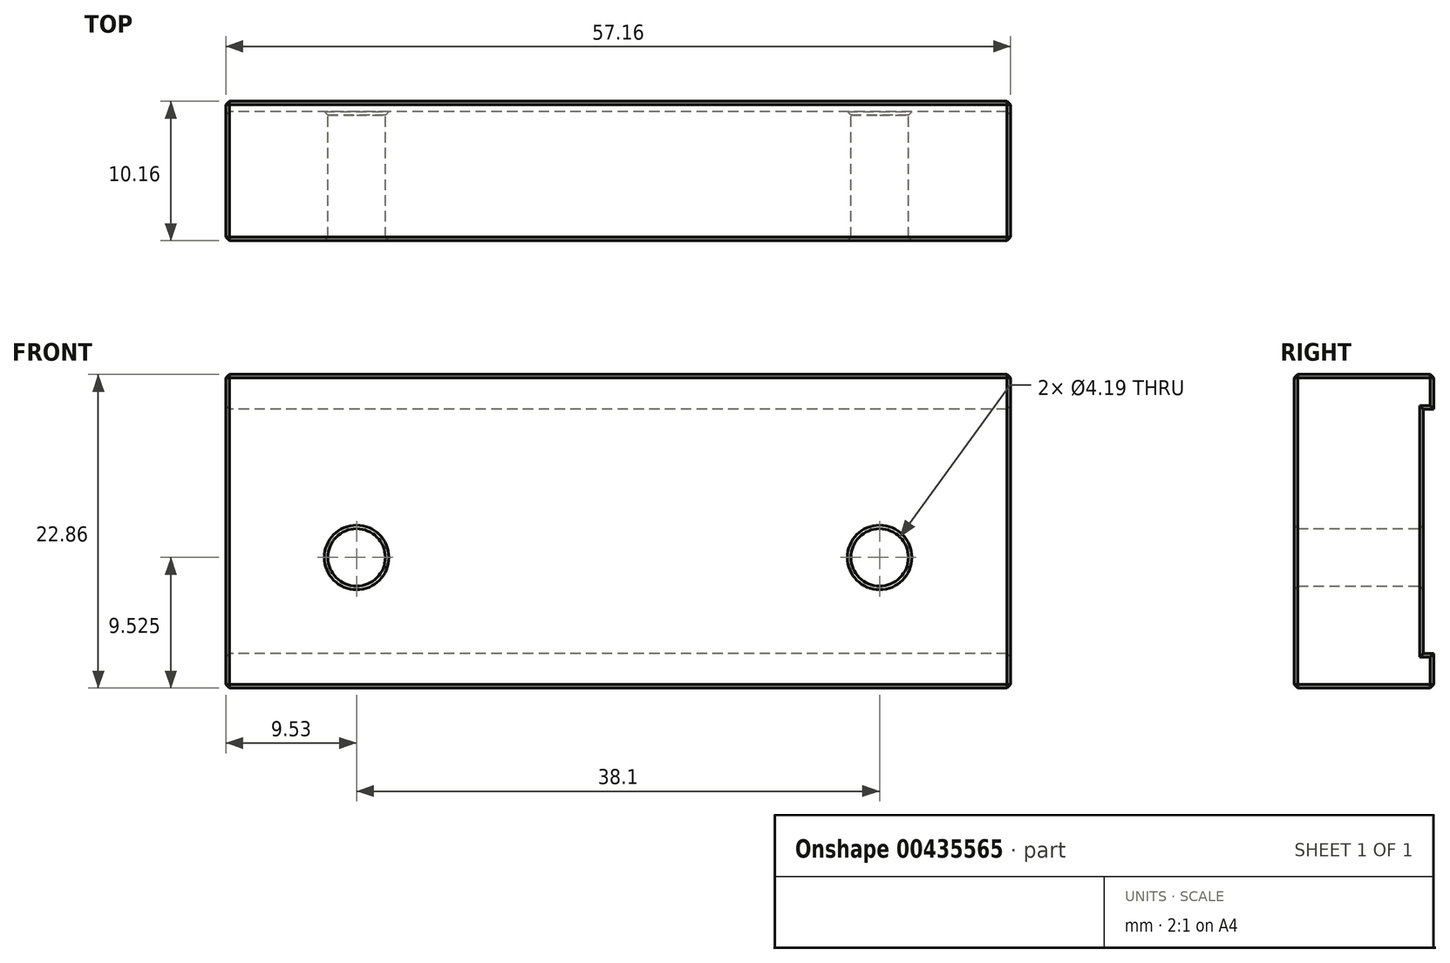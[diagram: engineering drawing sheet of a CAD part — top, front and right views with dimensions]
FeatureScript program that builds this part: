
annotation { "Feature Type Name" : "Feature", "Feature Type Description" : "" }
export const myFeature = defineFeature(function(context is Context, id is Id, definition is map)
    precondition{}
    {
        {
            var Q0;
            Q0=qCreatedBy(makeId("Front.planeOp"),FACE);
            var sketch = newSketch(context, id + "F0", { "sketchPlane" : qUnion([Q0])});
            skLineSegment(sketch, "E0.bottom", {"start": v(28.58, -11.43) * mm, "end": v(-28.58, -11.43) * mm});
            skLineSegment(sketch, "E0.top", {"start": v(28.58, 11.43) * mm, "end": v(-28.58, 11.43) * mm});
            skLineSegment(sketch, "E0.left", {"start": v(28.58, -11.43) * mm, "end": v(28.58, 11.43) * mm});
            skLineSegment(sketch, "E0.right", {"start": v(-28.58, -11.43) * mm, "end": v(-28.58, 11.43) * mm});
            skPoint(sketch, "E0.middle", {"position": v(0, 0) * mm});
            skCircle(sketch, "E1", {"center": v(-19.05, -1.9) * mm, "radius": 2.1 * mm});
            skCircle(sketch, "E2.MirrorC", {"center": v(19.05, -1.9) * mm, "radius": 2.1 * mm});
            skSolve(sketch);
        }
        {
            var Q0;
            Q0=makeQuery(id+"F0.imprint","IMPRINT",FACE,{"disambiguationData":[TD([[makeQuery(id+"F0.imprint","IMPRINT",EDGE,{"derivedFrom":sQuery(id+"F0.wireOp",EDGE,"E0.bottom")}),-1.0]])]});
            extrude(context, id + "F1", {"entities" : qUnion([Q0]), "depth" : 9.4 * mm});
        }
        {
            var Q0;
            Q0=makeQuery(id+"F1.opExtrude","CAP_FACE",FACE,{"disambiguationData":[OSD([sQuery(id+"F0.wireOp",EDGE,"E0.bottom"),sQuery(id+"F0.wireOp",EDGE,"E0.top"),sQuery(id+"F0.wireOp",EDGE,"E0.left"),sQuery(id+"F0.wireOp",EDGE,"E0.right"),sQuery(id+"F0.wireOp",EDGE,"E1"),sQuery(id+"F0.wireOp",EDGE,"E2.MirrorC")])],"isStart":true});
            var sketch = newSketch(context, id + "F2", { "sketchPlane" : qUnion([Q0])});
            skLineSegment(sketch, "E3.bottom", {"start": v(-28.58, -11.43) * mm, "end": v(28.58, -11.43) * mm});
            skLineSegment(sketch, "E3.top", {"start": v(-28.58, -8.9) * mm, "end": v(28.58, -8.9) * mm});
            skLineSegment(sketch, "E3.left", {"start": v(-28.58, -11.43) * mm, "end": v(-28.58, -8.9) * mm});
            skLineSegment(sketch, "E3.right", {"start": v(28.58, -11.43) * mm, "end": v(28.58, -8.9) * mm});
            skSolve(sketch);
        }
        {
            var Q0;
            Q0 = qSketchRegion(id + "F2", true);
            extrude(context, id + "F3", {"entities" : qUnion([Q0]), "operationType" : NewBodyOperationType.ADD, "depth" : 0.76 * mm});
        }
        {
            var Q0;
            Q0=makeQuery(id+"F1.opExtrude","CAP_FACE",FACE,{"disambiguationData":[OSD([sQuery(id+"F0.wireOp",EDGE,"E0.bottom"),sQuery(id+"F0.wireOp",EDGE,"E0.top"),sQuery(id+"F0.wireOp",EDGE,"E0.left"),sQuery(id+"F0.wireOp",EDGE,"E0.right"),sQuery(id+"F0.wireOp",EDGE,"E1"),sQuery(id+"F0.wireOp",EDGE,"E2.MirrorC")])],"isStart":true});
            var sketch = newSketch(context, id + "F4", { "sketchPlane" : qUnion([Q0])});
            skLineSegment(sketch, "E4.bottom", {"start": v(-28.58, 11.43) * mm, "end": v(28.58, 11.43) * mm});
            skLineSegment(sketch, "E4.top", {"start": v(-28.58, 8.9) * mm, "end": v(28.58, 8.9) * mm});
            skLineSegment(sketch, "E4.left", {"start": v(-28.58, 11.43) * mm, "end": v(-28.58, 8.9) * mm});
            skLineSegment(sketch, "E4.right", {"start": v(28.58, 11.43) * mm, "end": v(28.58, 8.9) * mm});
            skSolve(sketch);
        }
        {
            var Q0;
            Q0 = qSketchRegion(id + "F4", true);
            extrude(context, id + "F5", {"entities" : qUnion([Q0]), "operationType" : NewBodyOperationType.ADD, "depth" : 0.76 * mm});
        }
        {
            var Q0;
            Q0=makeQuery(id+"F1.opExtrude","CAP_EDGE",EDGE,{"disambiguationData":[OSD([sQuery(id+"F0.wireOp",EDGE,"E0.left")])],"isStart":true});
            var Q1;
            Q1=makeQuery(id+"F5.boolean.opBoolean","MERGE",EDGE,{"derivedFrom":[makeQuery(id+"F1.opExtrude","SWEPT_EDGE",EDGE,{"disambiguationData":[OSD([sQuery(id+"F0.wireOp",EDGE,"E0.top"),sQuery(id+"F0.wireOp",EDGE,"E0.right")])]}),makeQuery(id+"F5.opExtrude","SWEPT_EDGE",EDGE,{"disambiguationData":[OSD([sQuery(id+"F4.wireOp",EDGE,"E4.bottom"),sQuery(id+"F4.wireOp",EDGE,"E4.right")])]})]});
            var Q2;
            Q2=makeQuery(id+"F5.boolean.opBoolean","MERGE",EDGE,{"derivedFrom":[makeQuery(id+"F1.opExtrude","SWEPT_EDGE",EDGE,{"disambiguationData":[OSD([sQuery(id+"F0.wireOp",EDGE,"E0.top"),sQuery(id+"F0.wireOp",EDGE,"E0.left")])]}),makeQuery(id+"F5.opExtrude","SWEPT_EDGE",EDGE,{"disambiguationData":[OSD([sQuery(id+"F4.wireOp",EDGE,"E4.bottom"),sQuery(id+"F4.wireOp",EDGE,"E4.left")])]})]});
            var Q3;
            Q3=makeQuery(id+"F5.opExtrude","CAP_EDGE",EDGE,{"disambiguationData":[OSD([sQuery(id+"F4.wireOp",EDGE,"E4.bottom")])],"isStart":false});
            var Q4;
            Q4=makeQuery(id+"F1.opExtrude","CAP_EDGE",EDGE,{"disambiguationData":[OSD([sQuery(id+"F0.wireOp",EDGE,"E1")])],"isStart":false});
            var Q5;
            Q5=makeQuery(id+"F1.opExtrude","CAP_EDGE",EDGE,{"disambiguationData":[OSD([sQuery(id+"F0.wireOp",EDGE,"E2.MirrorC")])],"isStart":false});
            var Q6;
            Q6=makeQuery(id+"F1.opExtrude","CAP_EDGE",EDGE,{"disambiguationData":[OSD([sQuery(id+"F0.wireOp",EDGE,"E0.bottom")])],"isStart":false});
            var Q7;
            Q7=makeQuery(id+"F1.opExtrude","CAP_EDGE",EDGE,{"disambiguationData":[OSD([sQuery(id+"F0.wireOp",EDGE,"E0.top")])],"isStart":false});
            var Q8;
            Q8=makeQuery(id+"F1.opExtrude","CAP_EDGE",EDGE,{"disambiguationData":[OSD([sQuery(id+"F0.wireOp",EDGE,"E0.left")])],"isStart":false});
            var Q9;
            Q9=makeQuery(id+"F1.opExtrude","CAP_EDGE",EDGE,{"disambiguationData":[OSD([sQuery(id+"F0.wireOp",EDGE,"E0.right")])],"isStart":false});
            var Q10;
            Q10=makeQuery(id+"F3.boolean.opBoolean","MERGE",EDGE,{"derivedFrom":[makeQuery(id+"F1.opExtrude","SWEPT_EDGE",EDGE,{"disambiguationData":[OSD([sQuery(id+"F0.wireOp",EDGE,"E0.bottom"),sQuery(id+"F0.wireOp",EDGE,"E0.left")])]}),makeQuery(id+"F3.opExtrude","SWEPT_EDGE",EDGE,{"disambiguationData":[OSD([sQuery(id+"F2.wireOp",EDGE,"E3.bottom"),sQuery(id+"F2.wireOp",EDGE,"E3.left")])]})]});
            var Q11;
            Q11=makeQuery(id+"F1.opExtrude","CAP_EDGE",EDGE,{"disambiguationData":[OSD([sQuery(id+"F0.wireOp",EDGE,"E0.right")])],"isStart":true});
            var Q12;
            Q12=makeQuery(id+"F5.opExtrude","CAP_EDGE",EDGE,{"disambiguationData":[OSD([sQuery(id+"F4.wireOp",EDGE,"E4.left")])],"isStart":false});
            var Q13;
            Q13=makeQuery(id+"F5.opExtrude","SWEPT_EDGE",EDGE,{"disambiguationData":[OSD([sQuery(id+"F0.wireOp",EDGE,"E0.left"),sQuery(id+"F4.wireOp",EDGE,"E4.top"),sQuery(id+"F4.wireOp",EDGE,"E4.left")])]});
            var Q14;
            Q14=makeQuery(id+"F3.boolean.opBoolean","MERGE",EDGE,{"derivedFrom":[makeQuery(id+"F1.opExtrude","SWEPT_EDGE",EDGE,{"disambiguationData":[OSD([sQuery(id+"F0.wireOp",EDGE,"E0.bottom"),sQuery(id+"F0.wireOp",EDGE,"E0.right")])]}),makeQuery(id+"F3.opExtrude","SWEPT_EDGE",EDGE,{"disambiguationData":[OSD([sQuery(id+"F2.wireOp",EDGE,"E3.bottom"),sQuery(id+"F2.wireOp",EDGE,"E3.right")])]})]});
            var Q15;
            Q15=makeQuery(id+"F1.opExtrude","CAP_EDGE",EDGE,{"disambiguationData":[OSD([sQuery(id+"F0.wireOp",EDGE,"E2.MirrorC")])],"isStart":true});
            var Q16;
            Q16=makeQuery(id+"F3.opExtrude","SWEPT_EDGE",EDGE,{"disambiguationData":[OSD([sQuery(id+"F0.wireOp",EDGE,"E0.left"),sQuery(id+"F2.wireOp",EDGE,"E3.top"),sQuery(id+"F2.wireOp",EDGE,"E3.left")])]});
            var Q17;
            Q17=makeQuery(id+"F1.opExtrude","CAP_EDGE",EDGE,{"disambiguationData":[OSD([sQuery(id+"F0.wireOp",EDGE,"E1")])],"isStart":true});
            var Q18;
            Q18=makeQuery(id+"F3.opExtrude","CAP_EDGE",EDGE,{"disambiguationData":[OSD([sQuery(id+"F2.wireOp",EDGE,"E3.left")])],"isStart":false});
            var Q19;
            Q19=makeQuery(id+"F3.opExtrude","CAP_EDGE",EDGE,{"disambiguationData":[OSD([sQuery(id+"F2.wireOp",EDGE,"E3.bottom")])],"isStart":false});
            var Q20;
            Q20=makeQuery(id+"F5.opExtrude","CAP_EDGE",EDGE,{"disambiguationData":[OSD([sQuery(id+"F4.wireOp",EDGE,"E4.right")])],"isStart":false});
            var Q21;
            Q21=makeQuery(id+"F5.opExtrude","SWEPT_EDGE",EDGE,{"disambiguationData":[OSD([sQuery(id+"F0.wireOp",EDGE,"E0.right"),sQuery(id+"F4.wireOp",EDGE,"E4.top"),sQuery(id+"F4.wireOp",EDGE,"E4.right")])]});
            var Q22;
            Q22=makeQuery(id+"F3.opExtrude","CAP_EDGE",EDGE,{"disambiguationData":[OSD([sQuery(id+"F2.wireOp",EDGE,"E3.right")])],"isStart":false});
            var Q23;
            Q23=makeQuery(id+"F3.opExtrude","SWEPT_EDGE",EDGE,{"disambiguationData":[OSD([sQuery(id+"F0.wireOp",EDGE,"E0.right"),sQuery(id+"F2.wireOp",EDGE,"E3.top"),sQuery(id+"F2.wireOp",EDGE,"E3.right")])]});
            var Q24;
            Q24=makeQuery(id+"F1.opExtrude","CAP_FACE",FACE,{"disambiguationData":[OSD([sQuery(id+"F0.wireOp",EDGE,"E0.bottom"),sQuery(id+"F0.wireOp",EDGE,"E0.top"),sQuery(id+"F0.wireOp",EDGE,"E0.left"),sQuery(id+"F0.wireOp",EDGE,"E0.right"),sQuery(id+"F0.wireOp",EDGE,"E1"),sQuery(id+"F0.wireOp",EDGE,"E2.MirrorC")])],"isStart":false});
            chamfer(context, id + "F6", {"entities" : qUnion([Q0, Q1, Q2, Q3, Q4, Q5, Q6, Q7, Q8, Q9, Q10, Q11, Q12, Q13, Q14, Q15, Q16, Q17, Q18, Q19, Q20, Q21, Q22, Q23, Q24]), "width" : 0.25 * mm, "tangentPropagation" : true});
        }
    });
